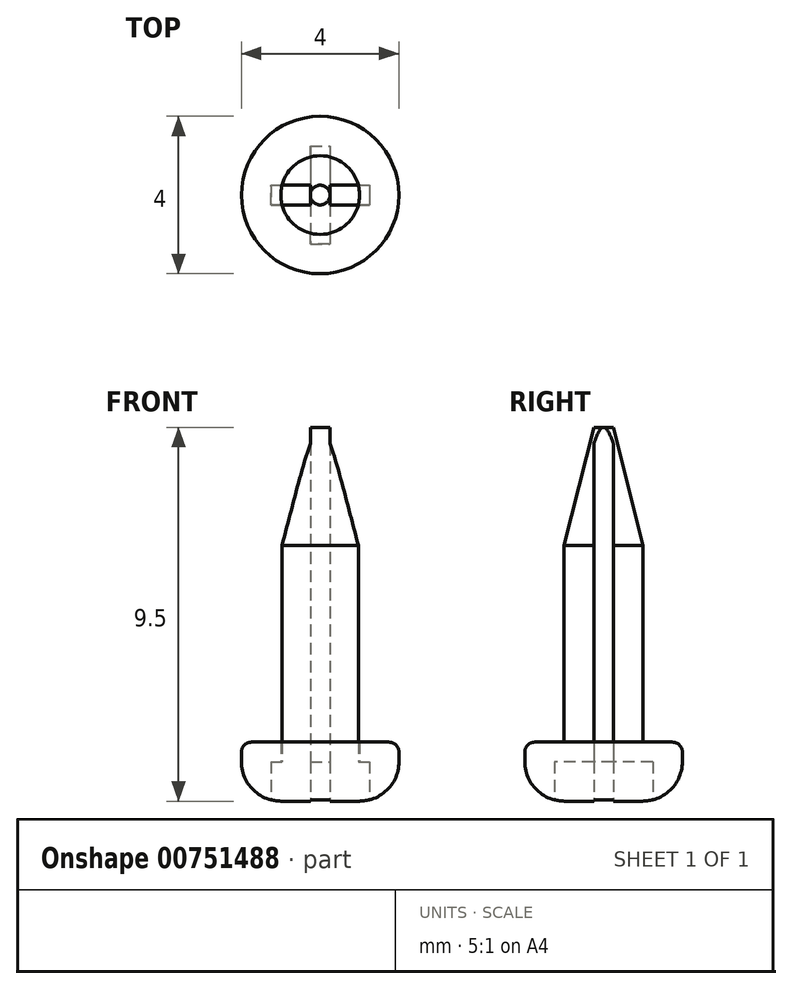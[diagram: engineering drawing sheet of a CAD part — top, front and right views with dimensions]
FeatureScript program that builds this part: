
annotation { "Feature Type Name" : "Feature", "Feature Type Description" : "" }
export const myFeature = defineFeature(function(context is Context, id is Id, definition is map)
    precondition{}
    {
        {
            var Q0;
            Q0=qCreatedBy(makeId("Top.planeOp"),FACE);
            var sketch = newSketch(context, id + "F0", { "sketchPlane" : qUnion([Q0])});
            skCircle(sketch, "E0", {"center": v(0, 0) * mm, "radius": 2 * mm});
            skCircle(sketch, "E1", {"center": v(0, 0) * mm, "radius": 1 * mm});
            skLineSegment(sketch, "E2.bottom", {"start": v(-0.25, 1.25) * mm, "end": v(0.25, 1.25) * mm});
            skLineSegment(sketch, "E2.top", {"start": v(-0.25, -1.25) * mm, "end": v(0.25, -1.25) * mm});
            skLineSegment(sketch, "E2.left", {"start": v(-0.25, 1.25) * mm, "end": v(-0.25, -1.25) * mm});
            skLineSegment(sketch, "E2.right", {"start": v(0.25, 1.25) * mm, "end": v(0.25, -1.25) * mm});
            skLineSegment(sketch, "E3.bottom", {"start": v(-1.25, 0.25) * mm, "end": v(1.25, 0.25) * mm});
            skLineSegment(sketch, "E3.top", {"start": v(-1.25, -0.25) * mm, "end": v(1.25, -0.25) * mm});
            skLineSegment(sketch, "E3.left", {"start": v(-1.25, 0.25) * mm, "end": v(-1.25, -0.25) * mm});
            skLineSegment(sketch, "E3.right", {"start": v(1.25, 0.25) * mm, "end": v(1.25, -0.25) * mm});
            skSolve(sketch);
        }
        {
            var Q0;
            Q0=makeQuery(id+"F0.imprint","IMPRINT",FACE,{"disambiguationData":[TD([[makeQuery(id+"F0.imprint","IMPRINT",EDGE,{"derivedFrom":sQuery(id+"F0.wireOp",EDGE,"E0")}),1.0]])]});
            var Q1;
            {var subQ0=sQuery(id+"F0.wireOp",EDGE,"E2.left");var subQ1=sQuery(id+"F0.wireOp",EDGE,"E1");var subQ2=makeQuery(id+"F0.imprint","INTERSECT",VERTEX,{"disambiguationData":[OD(0.0)],"derivedFrom":[subQ1,subQ0]});Q1=makeQuery(id+"F0.imprint","IMPRINT",FACE,{"disambiguationData":[TD([[makeQuery(id+"F0.imprint","IMPRINT",EDGE,{"disambiguationData":[TD([[subQ2,-1.0]])],"derivedFrom":subQ1}),1.0]])]});}
            var Q2;
            {var subQ0=sQuery(id+"F0.wireOp",EDGE,"E3.top");var subQ1=sQuery(id+"F0.wireOp",EDGE,"E1");var subQ2=makeQuery(id+"F0.imprint","INTERSECT",VERTEX,{"disambiguationData":[OD(0.0)],"derivedFrom":[subQ1,subQ0]});Q2=makeQuery(id+"F0.imprint","IMPRINT",FACE,{"disambiguationData":[TD([[makeQuery(id+"F0.imprint","IMPRINT",EDGE,{"disambiguationData":[TD([[subQ2,-1.0]])],"derivedFrom":subQ1}),1.0]])]});}
            var Q3;
            {var subQ0=sQuery(id+"F0.wireOp",EDGE,"E2.right");var subQ1=sQuery(id+"F0.wireOp",EDGE,"E1");var subQ2=makeQuery(id+"F0.imprint","INTERSECT",VERTEX,{"disambiguationData":[OD(1.0)],"derivedFrom":[subQ1,subQ0]});Q3=makeQuery(id+"F0.imprint","IMPRINT",FACE,{"disambiguationData":[TD([[makeQuery(id+"F0.imprint","IMPRINT",EDGE,{"disambiguationData":[TD([[subQ2,-1.0]])],"derivedFrom":subQ1}),1.0]])]});}
            var Q4;
            {var subQ0=sQuery(id+"F0.wireOp",EDGE,"E2.right");var subQ1=sQuery(id+"F0.wireOp",EDGE,"E1");var subQ2=makeQuery(id+"F0.imprint","INTERSECT",VERTEX,{"disambiguationData":[OD(0.0)],"derivedFrom":[subQ1,subQ0]});Q4=makeQuery(id+"F0.imprint","IMPRINT",FACE,{"disambiguationData":[TD([[makeQuery(id+"F0.imprint","IMPRINT",EDGE,{"disambiguationData":[TD([[subQ2,1.0]])],"derivedFrom":subQ1}),1.0]])]});}
            extrude(context, id + "F1", {"entities" : qUnion([Q0, Q1, Q2, Q3, Q4]), "depth" : 1 * mm, "offsetDistance" : 25 * mm});
        }
        {
            var Q0;
            {var subQ5=sQuery(id+"F0.wireOp",EDGE,"E3.left");Q0=makeQuery(id+"F0.imprint","IMPRINT",FACE,{"disambiguationData":[TD([[makeQuery(id+"F0.imprint","IMPRINT",EDGE,{"derivedFrom":subQ5}),1.0]])]});}
            var Q1;
            {var subQ0=sQuery(id+"F0.wireOp",EDGE,"E3.top");var subQ1=sQuery(id+"F0.wireOp",EDGE,"E1");var subQ2=makeQuery(id+"F0.imprint","INTERSECT",VERTEX,{"disambiguationData":[OD(0.0)],"derivedFrom":[subQ1,subQ0]});Q1=makeQuery(id+"F0.imprint","IMPRINT",FACE,{"disambiguationData":[TD([[makeQuery(id+"F0.imprint","IMPRINT",EDGE,{"disambiguationData":[TD([[subQ2,-1.0]])],"derivedFrom":subQ1}),1.0]])]});}
            var Q2;
            {var subQ0=sQuery(id+"F0.wireOp",EDGE,"E2.right");var subQ1=sQuery(id+"F0.wireOp",EDGE,"E1");var subQ2=makeQuery(id+"F0.imprint","INTERSECT",VERTEX,{"disambiguationData":[OD(1.0)],"derivedFrom":[subQ1,subQ0]});Q2=makeQuery(id+"F0.imprint","IMPRINT",FACE,{"disambiguationData":[TD([[makeQuery(id+"F0.imprint","IMPRINT",EDGE,{"disambiguationData":[TD([[subQ2,-1.0]])],"derivedFrom":subQ1}),1.0]])]});}
            var Q3;
            {var subQ0=sQuery(id+"F0.wireOp",EDGE,"E2.right");var subQ1=sQuery(id+"F0.wireOp",EDGE,"E1");var subQ2=makeQuery(id+"F0.imprint","INTERSECT",VERTEX,{"disambiguationData":[OD(0.0)],"derivedFrom":[subQ1,subQ0]});Q3=makeQuery(id+"F0.imprint","IMPRINT",FACE,{"disambiguationData":[TD([[makeQuery(id+"F0.imprint","IMPRINT",EDGE,{"disambiguationData":[TD([[subQ2,-1.0]])],"derivedFrom":subQ1}),1.0]])]});}
            var Q4;
            {var subQ5=sQuery(id+"F0.wireOp",EDGE,"E3.right");Q4=makeQuery(id+"F0.imprint","IMPRINT",FACE,{"disambiguationData":[TD([[makeQuery(id+"F0.imprint","IMPRINT",EDGE,{"derivedFrom":subQ5}),-1.0]])]});}
            var Q5;
            {var subQ0=sQuery(id+"F0.wireOp",EDGE,"E2.left");var subQ1=sQuery(id+"F0.wireOp",EDGE,"E1");var subQ2=makeQuery(id+"F0.imprint","INTERSECT",VERTEX,{"disambiguationData":[OD(1.0)],"derivedFrom":[subQ1,subQ0]});Q5=makeQuery(id+"F0.imprint","IMPRINT",FACE,{"disambiguationData":[TD([[makeQuery(id+"F0.imprint","IMPRINT",EDGE,{"disambiguationData":[TD([[subQ2,-1.0]])],"derivedFrom":subQ1}),1.0]])]});}
            var Q6;
            {var subQ0=sQuery(id+"F0.wireOp",EDGE,"E3.bottom");var subQ1=sQuery(id+"F0.wireOp",EDGE,"E1");var subQ2=makeQuery(id+"F0.imprint","INTERSECT",VERTEX,{"disambiguationData":[OD(0.0)],"derivedFrom":[subQ1,subQ0]});Q6=makeQuery(id+"F0.imprint","IMPRINT",FACE,{"disambiguationData":[TD([[makeQuery(id+"F0.imprint","IMPRINT",EDGE,{"disambiguationData":[TD([[subQ2,1.0]])],"derivedFrom":subQ1}),1.0]])]});}
            var Q7;
            {var subQ0=sQuery(id+"F0.wireOp",EDGE,"E2.right");var subQ1=sQuery(id+"F0.wireOp",EDGE,"E1");var subQ2=makeQuery(id+"F0.imprint","INTERSECT",VERTEX,{"disambiguationData":[OD(0.0)],"derivedFrom":[subQ1,subQ0]});Q7=makeQuery(id+"F0.imprint","IMPRINT",FACE,{"disambiguationData":[TD([[makeQuery(id+"F0.imprint","IMPRINT",EDGE,{"disambiguationData":[TD([[subQ2,1.0]])],"derivedFrom":subQ1}),1.0]])]});}
            var Q8;
            {var subQ0=sQuery(id+"F0.wireOp",EDGE,"E2.left");var subQ1=sQuery(id+"F0.wireOp",EDGE,"E1");var subQ2=makeQuery(id+"F0.imprint","INTERSECT",VERTEX,{"disambiguationData":[OD(0.0)],"derivedFrom":[subQ1,subQ0]});Q8=makeQuery(id+"F0.imprint","IMPRINT",FACE,{"disambiguationData":[TD([[makeQuery(id+"F0.imprint","IMPRINT",EDGE,{"disambiguationData":[TD([[subQ2,-1.0]])],"derivedFrom":subQ1}),1.0]])]});}
            var Q9;
            {var subQ0=sQuery(id+"F0.wireOp",EDGE,"E3.bottom");var subQ1=sQuery(id+"F0.wireOp",EDGE,"E1");var subQ2=makeQuery(id+"F0.imprint","INTERSECT",VERTEX,{"disambiguationData":[OD(1.0)],"derivedFrom":[subQ1,subQ0]});Q9=makeQuery(id+"F0.imprint","IMPRINT",FACE,{"disambiguationData":[TD([[makeQuery(id+"F0.imprint","IMPRINT",EDGE,{"disambiguationData":[TD([[subQ2,-1.0]])],"derivedFrom":subQ1}),1.0]])]});}
            var Q10;
            {var subQ5=sQuery(id+"F0.wireOp",EDGE,"E2.bottom");Q10=makeQuery(id+"F0.imprint","IMPRINT",FACE,{"disambiguationData":[TD([[makeQuery(id+"F0.imprint","IMPRINT",EDGE,{"derivedFrom":subQ5}),-1.0]])]});}
            var Q11;
            {var subQ5=sQuery(id+"F0.wireOp",EDGE,"E2.top");Q11=makeQuery(id+"F0.imprint","IMPRINT",FACE,{"disambiguationData":[TD([[makeQuery(id+"F0.imprint","IMPRINT",EDGE,{"derivedFrom":subQ5}),1.0]])]});}
            var Q12;
            {var subQ0=sQuery(id+"F0.wireOp",EDGE,"E3.bottom");var subQ1=sQuery(id+"F0.wireOp",EDGE,"E2.left");var subQ2=makeQuery(id+"F0.imprint","INTERSECT",VERTEX,{"derivedFrom":[subQ1,subQ0]});Q12=makeQuery(id+"F0.imprint","IMPRINT",FACE,{"disambiguationData":[TD([[makeQuery(id+"F0.imprint","IMPRINT",EDGE,{"disambiguationData":[TD([[subQ2,-1.0]])],"derivedFrom":subQ1}),1.0]])]});}
            var Q13;
            Q13=makeQuery(id+"F0.imprint","IMPRINT",FACE,{"disambiguationData":[TD([[makeQuery(id+"F0.imprint","IMPRINT",EDGE,{"derivedFrom":sQuery(id+"F0.wireOp",EDGE,"E0")}),1.0]])]});
            extrude(context, id + "F2", {"entities" : qUnion([Q0, Q1, Q2, Q3, Q4, Q5, Q6, Q7, Q8, Q9, Q10, Q11, Q12, Q13]), "operationType" : NewBodyOperationType.ADD, "depth" : 1.5 * mm, "offsetDistance" : 25 * mm, "hasSecondDirection" : true, "secondDirectionOppositeDirection" : false, "secondDirectionDepth" : 1 * mm});
        }
        {
            var Q0;
            {var subQ0=sQuery(id+"F0.wireOp",EDGE,"E3.top");var subQ1=sQuery(id+"F0.wireOp",EDGE,"E1");var subQ2=makeQuery(id+"F0.imprint","INTERSECT",VERTEX,{"disambiguationData":[OD(0.0)],"derivedFrom":[subQ1,subQ0]});Q0=makeQuery(id+"F0.imprint","IMPRINT",FACE,{"disambiguationData":[TD([[makeQuery(id+"F0.imprint","IMPRINT",EDGE,{"disambiguationData":[TD([[subQ2,-1.0]])],"derivedFrom":subQ1}),1.0]])]});}
            var Q1;
            {var subQ0=sQuery(id+"F0.wireOp",EDGE,"E3.bottom");var subQ1=sQuery(id+"F0.wireOp",EDGE,"E1");var subQ2=makeQuery(id+"F0.imprint","INTERSECT",VERTEX,{"disambiguationData":[OD(1.0)],"derivedFrom":[subQ1,subQ0]});Q1=makeQuery(id+"F0.imprint","IMPRINT",FACE,{"disambiguationData":[TD([[makeQuery(id+"F0.imprint","IMPRINT",EDGE,{"disambiguationData":[TD([[subQ2,-1.0]])],"derivedFrom":subQ1}),1.0]])]});}
            var Q2;
            {var subQ0=sQuery(id+"F0.wireOp",EDGE,"E2.left");var subQ1=sQuery(id+"F0.wireOp",EDGE,"E1");var subQ2=makeQuery(id+"F0.imprint","INTERSECT",VERTEX,{"disambiguationData":[OD(0.0)],"derivedFrom":[subQ1,subQ0]});Q2=makeQuery(id+"F0.imprint","IMPRINT",FACE,{"disambiguationData":[TD([[makeQuery(id+"F0.imprint","IMPRINT",EDGE,{"disambiguationData":[TD([[subQ2,-1.0]])],"derivedFrom":subQ1}),1.0]])]});}
            var Q3;
            {var subQ0=sQuery(id+"F0.wireOp",EDGE,"E2.right");var subQ1=sQuery(id+"F0.wireOp",EDGE,"E1");var subQ2=makeQuery(id+"F0.imprint","INTERSECT",VERTEX,{"disambiguationData":[OD(0.0)],"derivedFrom":[subQ1,subQ0]});Q3=makeQuery(id+"F0.imprint","IMPRINT",FACE,{"disambiguationData":[TD([[makeQuery(id+"F0.imprint","IMPRINT",EDGE,{"disambiguationData":[TD([[subQ2,-1.0]])],"derivedFrom":subQ1}),1.0]])]});}
            var Q4;
            {var subQ0=sQuery(id+"F0.wireOp",EDGE,"E2.right");var subQ1=sQuery(id+"F0.wireOp",EDGE,"E1");var subQ2=makeQuery(id+"F0.imprint","INTERSECT",VERTEX,{"disambiguationData":[OD(0.0)],"derivedFrom":[subQ1,subQ0]});Q4=makeQuery(id+"F0.imprint","IMPRINT",FACE,{"disambiguationData":[TD([[makeQuery(id+"F0.imprint","IMPRINT",EDGE,{"disambiguationData":[TD([[subQ2,1.0]])],"derivedFrom":subQ1}),1.0]])]});}
            var Q5;
            {var subQ0=sQuery(id+"F0.wireOp",EDGE,"E3.bottom");var subQ1=sQuery(id+"F0.wireOp",EDGE,"E1");var subQ2=makeQuery(id+"F0.imprint","INTERSECT",VERTEX,{"disambiguationData":[OD(0.0)],"derivedFrom":[subQ1,subQ0]});Q5=makeQuery(id+"F0.imprint","IMPRINT",FACE,{"disambiguationData":[TD([[makeQuery(id+"F0.imprint","IMPRINT",EDGE,{"disambiguationData":[TD([[subQ2,1.0]])],"derivedFrom":subQ1}),1.0]])]});}
            var Q6;
            {var subQ0=sQuery(id+"F0.wireOp",EDGE,"E2.left");var subQ1=sQuery(id+"F0.wireOp",EDGE,"E1");var subQ2=makeQuery(id+"F0.imprint","INTERSECT",VERTEX,{"disambiguationData":[OD(1.0)],"derivedFrom":[subQ1,subQ0]});Q6=makeQuery(id+"F0.imprint","IMPRINT",FACE,{"disambiguationData":[TD([[makeQuery(id+"F0.imprint","IMPRINT",EDGE,{"disambiguationData":[TD([[subQ2,-1.0]])],"derivedFrom":subQ1}),1.0]])]});}
            var Q7;
            {var subQ0=sQuery(id+"F0.wireOp",EDGE,"E2.right");var subQ1=sQuery(id+"F0.wireOp",EDGE,"E1");var subQ2=makeQuery(id+"F0.imprint","INTERSECT",VERTEX,{"disambiguationData":[OD(1.0)],"derivedFrom":[subQ1,subQ0]});Q7=makeQuery(id+"F0.imprint","IMPRINT",FACE,{"disambiguationData":[TD([[makeQuery(id+"F0.imprint","IMPRINT",EDGE,{"disambiguationData":[TD([[subQ2,-1.0]])],"derivedFrom":subQ1}),1.0]])]});}
            var Q8;
            {var subQ0=sQuery(id+"F0.wireOp",EDGE,"E3.bottom");var subQ1=sQuery(id+"F0.wireOp",EDGE,"E2.left");var subQ2=makeQuery(id+"F0.imprint","INTERSECT",VERTEX,{"derivedFrom":[subQ1,subQ0]});Q8=makeQuery(id+"F0.imprint","IMPRINT",FACE,{"disambiguationData":[TD([[makeQuery(id+"F0.imprint","IMPRINT",EDGE,{"disambiguationData":[TD([[subQ2,-1.0]])],"derivedFrom":subQ1}),1.0]])]});}
            extrude(context, id + "F3", {"entities" : qUnion([Q0, Q1, Q2, Q3, Q4, Q5, Q6, Q7, Q8]), "operationType" : NewBodyOperationType.ADD, "depth" : (8 + 1.5) * mm, "offsetDistance" : 25 * mm, "hasSecondDirection" : true, "secondDirectionOppositeDirection" : false, "secondDirectionDepth" : 1.5 * mm});
        }
        {
            var Q0;
            Q0=makeQuery(id+"F3.opExtrude","CAP_EDGE",EDGE,{"disambiguationData":[OSD([sQuery(id+"F0.wireOp",EDGE,"E1")])],"isStart":false});
            chamfer(context, id + "F4", {"entities" : qUnion([Q0]), "chamferType" : ChamferType.TWO_OFFSETS, "width1" : .75 * mm, "oppositeDirection" : false, "width2" : 3 * mm, "tangentPropagation" : true});
        }
        {
            var Q0;
            Q0=makeQuery(id+"F1.opExtrude","CAP_EDGE",EDGE,{"disambiguationData":[OSD([sQuery(id+"F0.wireOp",EDGE,"E0")])],"isStart":true});
            fillet(context, id + "F5", {"entities" : qUnion([Q0]), "radius" : 1 * mm, "tangentPropagation" : true, "allowEdgeOverflow" : false});
        }
        {
            var Q0;
            Q0=makeQuery(id+"F2.opExtrude","CAP_EDGE",EDGE,{"disambiguationData":[OSD([sQuery(id+"F0.wireOp",EDGE,"E0")])],"isStart":false});
            var Q1;
            Q1=makeQuery(id+"F3.opExtrude","CAP_EDGE",EDGE,{"disambiguationData":[OSD([sQuery(id+"F0.wireOp",EDGE,"E1")])],"isStart":true});
            fillet(context, id + "F6", {"entities" : qUnion([Q0, Q1]), "radius" : .25 * mm, "tangentPropagation" : true, "allowEdgeOverflow" : false});
        }
    });
